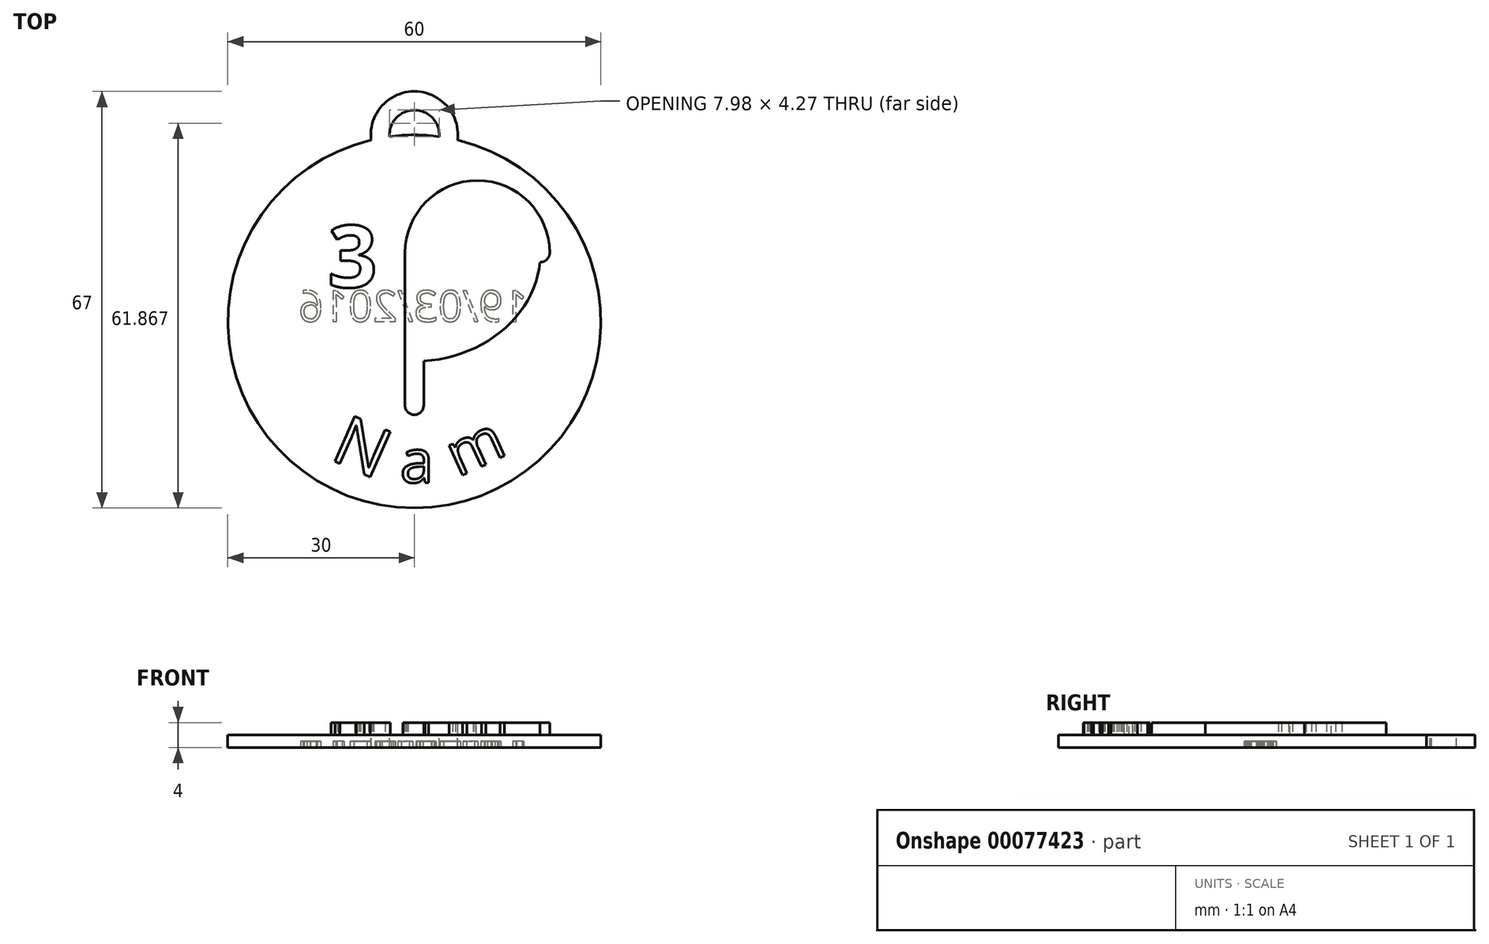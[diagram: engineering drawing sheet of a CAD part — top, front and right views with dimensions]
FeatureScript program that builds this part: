
annotation { "Feature Type Name" : "Feature", "Feature Type Description" : "" }
export const myFeature = defineFeature(function(context is Context, id is Id, definition is map)
    precondition{}
    {
        {
            var Q0;
            Q0=qCreatedBy(makeId("Top.planeOp"),FACE);
            var sketch = newSketch(context, id + "F0", { "sketchPlane" : qUnion([Q0])});
            skCircle(sketch, "E0", {"center": v(0, 0) * mm, "radius": 30 * mm});
            skSolve(sketch);
        }
        {
            var Q0;
            Q0=qSketchRegion(id+"F0",true);
            extrude(context, id + "F1", {"entities" : qUnion([Q0]), "oppositeDirection" : true, "depth" : 2 * mm});
        }
        {
            var Q0;
            Q0=qCreatedBy(makeId("Top.planeOp"),FACE);
            var sketch = newSketch(context, id + "F2", { "sketchPlane" : qUnion([Q0])});
            skEllipticalArc(sketch, "E1", {});
            skLineSegment(sketch, "E2", {"start": v(0, 0) * mm, "end": v(0, 30) * mm, "construction": true});
            skLineSegment(sketch, "E3", {"start": v(0, 11.04) * mm, "end": v(0, -13.5) * mm});
            skArc(sketch, "E4", {"start": v(20.27, 11.04) * mm, "mid": v(10.13, 21.17) * mm, "end": v(0, 11.04) * mm});
            skLineSegment(sketch, "E5", {"start": v(0, 11.04) * mm, "end": v(-16.84, 20.76) * mm, "construction": true});
            skLineSegment(sketch, "E6", {"start": v(0, 11.04) * mm, "end": v(-20.27, 11.04) * mm, "construction": true});
            skArc(sketch, "E7.0.startCap", {"start": v(-1.5, 11.04) * mm, "mid": v(0, 12.54) * mm, "end": v(1.5, 11.04) * mm});
            skArc(sketch, "E7.0.endCap", {"start": v(1.5, -13.5) * mm, "mid": v(0, -15) * mm, "end": v(-1.5, -13.5) * mm});
            skLineSegment(sketch, "E7.0.left", {"start": v(1.5, 11.04) * mm, "end": v(1.5, -13.5) * mm});
            skLineSegment(sketch, "E7.0.right", {"start": v(-1.5, 11.04) * mm, "end": v(-1.5, -13.5) * mm});
            skArc(sketch, "E8.0.startCap", {"start": v(21.77, 11.04) * mm, "mid": v(20.27, 9.54) * mm, "end": v(18.77, 11.04) * mm});
            skArc(sketch, "E8.0.endCap", {"start": v(1.5, 11.04) * mm, "mid": v(0, 9.54) * mm, "end": v(-1.5, 11.04) * mm});
            skArc(sketch, "E8.0.left", {"start": v(18.77, 11.04) * mm, "mid": v(10.13, 19.67) * mm, "end": v(1.5, 11.04) * mm});
            skArc(sketch, "E8.0.right", {"start": v(21.77, 11.04) * mm, "mid": v(10.13, 22.67) * mm, "end": v(-1.5, 11.04) * mm});
            skArc(sketch, "E8.1.startCap", {"start": v(-18.02, 21.68) * mm, "mid": v(-15.91, 21.95) * mm, "end": v(-15.65, 19.84) * mm});
            skArc(sketch, "E8.1.endCap", {"start": v(18.77, 11.04) * mm, "mid": v(20.27, 12.54) * mm, "end": v(21.77, 11.04) * mm});
            skFitSpline(sketch, "E8.1.left", {"points": [v(18.7, 9.5) * mm, v(18.8, 11.04) * mm, v(18.7, 12.6) * mm, v(18.36, 14.63) * mm, v(17.66, 16.6) * mm, v(16.63, 18.49) * mm, v(15.37, 20.3) * mm, v(13.44, 22.32) * mm, v(11.07, 24) * mm, v(8.94, 25.1) * mm, v(6.7, 26.01) * mm, v(4.32, 26.63) * mm, v(1.87, 26.95) * mm, v(0, 27.03) * mm, v(-1.87, 26.95) * mm, v(-4.32, 26.63) * mm, v(-6.7, 26.01) * mm, v(-8.94, 25.1) * mm, v(-11.07, 24) * mm, v(-13.44, 22.32) * mm, v(-15.37, 20.3) * mm, v(-16.63, 18.49) * mm, v(-17.66, 16.6) * mm, v(-18.36, 14.63) * mm, v(-18.7, 12.6) * mm, v(-18.8, 11.04) * mm, v(-18.7, 9.5) * mm, v(-18.36, 7.46) * mm, v(-17.66, 5.48) * mm, v(-16.63, 3.6) * mm, v(-15.37, 1.8) * mm, v(-13.44, -0.24) * mm, v(-11.07, -1.92) * mm, v(-8.94, -3.02) * mm, v(-6.7, -3.93) * mm, v(-4.32, -4.55) * mm, v(-1.87, -4.86) * mm, v(0, -4.94) * mm, v(1.87, -4.86) * mm, v(4.32, -4.55) * mm, v(6.7, -3.93) * mm, v(8.94, -3.02) * mm, v(11.07, -1.92) * mm, v(13.44, -0.24) * mm, v(15.37, 1.8) * mm, v(16.63, 3.6) * mm, v(17.66, 5.48) * mm, v(18.36, 7.46) * mm, v(18.7, 9.5) * mm, v(18.8, 11.04) * mm, v(18.7, 12.6) * mm]});
            skFitSpline(sketch, "E8.1.right", {"points": [v(21.7, 9.15) * mm, v(21.8, 11.04) * mm, v(21.7, 12.93) * mm, v(21.27, 15.42) * mm, v(20.42, 17.81) * mm, v(19.18, 20.07) * mm, v(17.69, 22.22) * mm, v(15.4, 24.61) * mm, v(12.65, 26.56) * mm, v(10.2, 27.83) * mm, v(7.62, 28.88) * mm, v(4.92, 29.58) * mm, v(2.12, 29.94) * mm, v(0, 30.03) * mm, v(-2.12, 29.94) * mm, v(-4.92, 29.58) * mm, v(-7.62, 28.88) * mm, v(-10.2, 27.83) * mm, v(-12.65, 26.56) * mm, v(-15.4, 24.61) * mm, v(-17.69, 22.22) * mm, v(-19.18, 20.07) * mm, v(-20.42, 17.81) * mm, v(-21.27, 15.42) * mm, v(-21.7, 12.93) * mm, v(-21.8, 11.04) * mm, v(-21.7, 9.15) * mm, v(-21.27, 6.67) * mm, v(-20.42, 4.27) * mm, v(-19.18, 2) * mm, v(-17.69, -0.14) * mm, v(-15.4, -2.53) * mm, v(-12.65, -4.48) * mm, v(-10.2, -5.75) * mm, v(-7.62, -6.8) * mm, v(-4.92, -7.5) * mm, v(-2.12, -7.86) * mm, v(0, -7.95) * mm, v(2.12, -7.86) * mm, v(4.92, -7.5) * mm, v(7.62, -6.8) * mm, v(10.2, -5.75) * mm, v(12.65, -4.48) * mm, v(15.4, -2.53) * mm, v(17.69, -0.14) * mm, v(19.18, 2) * mm, v(20.42, 4.27) * mm, v(21.27, 6.67) * mm, v(21.7, 9.15) * mm, v(21.8, 11.04) * mm, v(21.7, 12.93) * mm]});
            const initialGuessF2  = {"E1": [0, 0.011041626236194823, 1, 0, 0.020266667008310185, 0.017458373763805178, 2.5511335140588507, 0]};
            skSetInitialGuess(sketch, initialGuessF2);
            skSolve(sketch);
        }
        {
            var Q0;
            {var subQ0=sQuery(id+"F2.wireOp",EDGE,"E8.1.startCap");Q0=makeQuery(id+"F2.imprint","IMPRINT",FACE,{"disambiguationData":[TD([[makeQuery(id+"F2.imprint","IMPRINT",EDGE,{"derivedFrom":subQ0}),-1.0]])]});}
            var Q1;
            {var subQ0=sQuery(id+"F2.wireOp",EDGE,"E7.0.right");var subQ1=sQuery(id+"F2.wireOp",EDGE,"E1");var subQ2=makeQuery(id+"F2.imprint","INTERSECT",VERTEX,{"derivedFrom":[subQ1,subQ0]});Q1=makeQuery(id+"F2.imprint","IMPRINT",FACE,{"disambiguationData":[TD([[makeQuery(id+"F2.imprint","IMPRINT",EDGE,{"disambiguationData":[TD([[subQ2,-1.0]])],"derivedFrom":subQ1}),1.0]])]});}
            var Q2;
            {var subQ0=sQuery(id+"F2.wireOp",EDGE,"E3");var subQ1=sQuery(id+"F2.wireOp",EDGE,"E1");var subQ2=makeQuery(id+"F2.imprint","INTERSECT",VERTEX,{"derivedFrom":[subQ1,subQ0]});Q2=makeQuery(id+"F2.imprint","IMPRINT",FACE,{"disambiguationData":[TD([[makeQuery(id+"F2.imprint","IMPRINT",EDGE,{"disambiguationData":[TD([[subQ2,-1.0]])],"derivedFrom":subQ1}),1.0]])]});}
            var Q3;
            {var subQ0=sQuery(id+"F2.wireOp",EDGE,"E7.0.right");var subQ1=sQuery(id+"F2.wireOp",EDGE,"E1");var subQ2=makeQuery(id+"F2.imprint","INTERSECT",VERTEX,{"derivedFrom":[subQ1,subQ0]});Q3=makeQuery(id+"F2.imprint","IMPRINT",FACE,{"disambiguationData":[TD([[makeQuery(id+"F2.imprint","IMPRINT",EDGE,{"disambiguationData":[TD([[subQ2,-1.0]])],"derivedFrom":subQ1}),-1.0]])]});}
            var Q4;
            {var subQ0=sQuery(id+"F2.wireOp",EDGE,"E3");var subQ1=sQuery(id+"F2.wireOp",EDGE,"E1");var subQ2=makeQuery(id+"F2.imprint","INTERSECT",VERTEX,{"derivedFrom":[subQ1,subQ0]});Q4=makeQuery(id+"F2.imprint","IMPRINT",FACE,{"disambiguationData":[TD([[makeQuery(id+"F2.imprint","IMPRINT",EDGE,{"disambiguationData":[TD([[subQ2,-1.0]])],"derivedFrom":subQ1}),-1.0]])]});}
            var Q5;
            {var subQ0=sQuery(id+"F2.wireOp",EDGE,"E7.0.left");var subQ1=sQuery(id+"F2.wireOp",EDGE,"E1");var subQ2=makeQuery(id+"F2.imprint","INTERSECT",VERTEX,{"derivedFrom":[subQ1,subQ0]});Q5=makeQuery(id+"F2.imprint","IMPRINT",FACE,{"disambiguationData":[TD([[makeQuery(id+"F2.imprint","IMPRINT",EDGE,{"disambiguationData":[TD([[subQ2,-1.0]])],"derivedFrom":subQ1}),-1.0]])]});}
            var Q6;
            {var subQ0=sQuery(id+"F2.wireOp",EDGE,"E7.0.left");var subQ1=sQuery(id+"F2.wireOp",EDGE,"E1");var subQ2=makeQuery(id+"F2.imprint","INTERSECT",VERTEX,{"derivedFrom":[subQ1,subQ0]});Q6=makeQuery(id+"F2.imprint","IMPRINT",FACE,{"disambiguationData":[TD([[makeQuery(id+"F2.imprint","IMPRINT",EDGE,{"disambiguationData":[TD([[subQ2,-1.0]])],"derivedFrom":subQ1}),1.0]])]});}
            var Q7;
            {var subQ0=sQuery(id+"F2.wireOp",EDGE,"E4");var subQ1=sQuery(id+"F2.wireOp",EDGE,"E1");var subQ2=makeQuery(id+"F2.imprint","INTERSECT",VERTEX,{"derivedFrom":[subQ1,subQ0]});Q7=makeQuery(id+"F2.imprint","IMPRINT",FACE,{"disambiguationData":[TD([[makeQuery(id+"F2.imprint","IMPRINT",EDGE,{"disambiguationData":[TD([[subQ2,1.0]])],"derivedFrom":subQ1}),-1.0]])]});}
            var Q8;
            {var subQ0=sQuery(id+"F2.wireOp",EDGE,"E4");var subQ1=sQuery(id+"F2.wireOp",EDGE,"E1");var subQ2=makeQuery(id+"F2.imprint","INTERSECT",VERTEX,{"derivedFrom":[subQ1,subQ0]});Q8=makeQuery(id+"F2.imprint","IMPRINT",FACE,{"disambiguationData":[TD([[makeQuery(id+"F2.imprint","IMPRINT",EDGE,{"disambiguationData":[TD([[subQ2,1.0]])],"derivedFrom":subQ1}),1.0]])]});}
            var Q9;
            {var subQ5=sQuery(id+"F2.wireOp",EDGE,"E8.0.left");Q9=makeQuery(id+"F2.imprint","IMPRINT",FACE,{"disambiguationData":[TD([[makeQuery(id+"F2.imprint","IMPRINT",EDGE,{"derivedFrom":subQ5}),-1.0]])]});}
            var Q10;
            {var subQ5=sQuery(id+"F2.wireOp",EDGE,"E8.0.right");Q10=makeQuery(id+"F2.imprint","IMPRINT",FACE,{"disambiguationData":[TD([[makeQuery(id+"F2.imprint","IMPRINT",EDGE,{"derivedFrom":subQ5}),1.0]])]});}
            var Q11;
            {var subQ0=sQuery(id+"F2.wireOp",EDGE,"E4");var subQ1=sQuery(id+"F2.wireOp",EDGE,"E3");var subQ2=makeQuery(id+"F2.imprint","INTERSECT",VERTEX,{"derivedFrom":[subQ1,subQ0]});Q11=makeQuery(id+"F2.imprint","IMPRINT",FACE,{"disambiguationData":[TD([[makeQuery(id+"F2.imprint","IMPRINT",EDGE,{"disambiguationData":[TD([[subQ2,-1.0]])],"derivedFrom":subQ1}),-1.0]])]});}
            var Q12;
            {var subQ0=sQuery(id+"F2.wireOp",EDGE,"E4");var subQ1=sQuery(id+"F2.wireOp",EDGE,"E3");var subQ2=makeQuery(id+"F2.imprint","INTERSECT",VERTEX,{"derivedFrom":[subQ1,subQ0]});Q12=makeQuery(id+"F2.imprint","IMPRINT",FACE,{"disambiguationData":[TD([[makeQuery(id+"F2.imprint","IMPRINT",EDGE,{"disambiguationData":[TD([[subQ2,-1.0]])],"derivedFrom":subQ1}),1.0]])]});}
            var Q13;
            {var subQ0=sQuery(id+"F2.wireOp",EDGE,"E8.0.endCap");var subQ1=sQuery(id+"F2.wireOp",EDGE,"E3");var subQ2=makeQuery(id+"F2.imprint","INTERSECT",VERTEX,{"derivedFrom":[subQ1,subQ0]});Q13=makeQuery(id+"F2.imprint","IMPRINT",FACE,{"disambiguationData":[TD([[makeQuery(id+"F2.imprint","IMPRINT",EDGE,{"disambiguationData":[TD([[subQ2,-1.0]])],"derivedFrom":subQ1}),-1.0]])]});}
            var Q14;
            {var subQ0=sQuery(id+"F2.wireOp",EDGE,"E8.0.endCap");var subQ1=sQuery(id+"F2.wireOp",EDGE,"E3");var subQ2=makeQuery(id+"F2.imprint","INTERSECT",VERTEX,{"derivedFrom":[subQ1,subQ0]});Q14=makeQuery(id+"F2.imprint","IMPRINT",FACE,{"disambiguationData":[TD([[makeQuery(id+"F2.imprint","IMPRINT",EDGE,{"disambiguationData":[TD([[subQ2,-1.0]])],"derivedFrom":subQ1}),1.0]])]});}
            var Q15;
            {var subQ1=sQuery(id+"F2.wireOp",EDGE,"E7.0.endCap");Q15=makeQuery(id+"F2.imprint","IMPRINT",FACE,{"disambiguationData":[TD([[makeQuery(id+"F2.imprint","IMPRINT",EDGE,{"derivedFrom":subQ1}),-1.0]])]});}
            extrude(context, id + "F3", {"entities" : qUnion([Q0, Q1, Q2, Q3, Q4, Q5, Q6, Q7, Q8, Q9, Q10, Q11, Q12, Q13, Q14, Q15]), "operationType" : NewBodyOperationType.ADD, "depth" : 2 * mm});
        }
        {
            var Q0;
            Q0=qCreatedBy(makeId("Top.planeOp"),FACE);
            var sketch = newSketch(context, id + "F4", { "sketchPlane" : qUnion([Q0])});
            skText(sketch, "E9", { "text": "3", "fontName": "OpenSans-Bold.ttf"});
            skText(sketch, "E10", { "text": "D", "fontName": "OpenSans-Bold.ttf"});
            const initialGuessF4  = {"E9": [-0.0139, 0.0055, 1, 0, 0.01], "E10": [0.0055, 0.0055, 1, 0, 0.01]};
            skSetInitialGuess(sketch, initialGuessF4);
            skSolve(sketch);
        }
        {
            var Q0;
            Q0=qSketchRegion(id+"F4",true);
            extrude(context, id + "F5", {"entities" : qUnion([Q0]), "operationType" : NewBodyOperationType.ADD, "depth" : 2 * mm});
        }
        {
            var Q0;
            {var subQ8=sQuery(id+"F0.wireOp",EDGE,"E0");Q0=makeQuery(id+"F3.boolean.opBoolean","SPLIT",FACE,{"disambiguationData":[TD([makeQuery(id+"F1.opExtrude","SWEPT_FACE",FACE,{"disambiguationData":[OSD([subQ8])]})])],"derivedFrom":makeQuery(id+"F1.opExtrude","CAP_FACE",FACE,{"disambiguationData":[OSD([subQ8])],"isStart":true})});}
            var sketch = newSketch(context, id + "F6", { "sketchPlane" : qUnion([Q0])});
            skCircle(sketch, "E11.0", {"center": v(0, 0) * mm, "radius": 26 * mm, "construction": true});
            skText(sketch, "E12", { "text": "N", "fontName": "OpenSans-Regular.ttf"});
            skText(sketch, "E13", { "text": "a", "fontName": "OpenSans-Regular.ttf"});
            skText(sketch, "E14", { "text": "m", "fontName": "OpenSans-Regular.ttf"});
            const initialGuessF6  = {"E12": [-0.01377, -0.02205, 0.9141, -0.40551, 0.008], "E13": [-0.0023, -0.0259, 1, 0, 0.007], "E14": [0.007, -0.02504, 0.90827, 0.41838, 0.007]};
            skSetInitialGuess(sketch, initialGuessF6);
            skSolve(sketch);
        }
        {
            var Q0;
            Q0=qSketchRegion(id+"F6",true);
            extrude(context, id + "F7", {"entities" : qUnion([Q0]), "operationType" : NewBodyOperationType.ADD, "depth" : 2 * mm});
        }
        {
            var Q0;
            Q0=qCreatedBy(makeId("Top.planeOp"),FACE);
            var sketch = newSketch(context, id + "F8", { "sketchPlane" : qUnion([Q0])});
            skArc(sketch, "E15", {"start": v(5.48, 29.5) * mm, "mid": v(0, 35.5) * mm, "end": v(-5.48, 29.5) * mm});
            skArc(sketch, "E16.0.startCap", {"start": v(6.97, 29.36) * mm, "mid": v(5.34, 28) * mm, "end": v(3.98, 29.63) * mm});
            skArc(sketch, "E16.0.endCap", {"start": v(-3.98, 29.63) * mm, "mid": v(-5.34, 28) * mm, "end": v(-6.97, 29.36) * mm});
            skArc(sketch, "E16.0.left", {"start": v(3.98, 29.63) * mm, "mid": v(0, 34) * mm, "end": v(-3.98, 29.63) * mm});
            skArc(sketch, "E16.0.right", {"start": v(6.97, 29.36) * mm, "mid": v(0, 37) * mm, "end": v(-6.97, 29.36) * mm});
            skSolve(sketch);
        }
        {
            var Q0;
            Q0=qSketchRegion(id+"F8",true);
            extrude(context, id + "F9", {"entities" : qUnion([Q0]), "operationType" : NewBodyOperationType.ADD, "oppositeDirection" : true, "depth" : 2 * mm});
        }
        {
            var Q0;
            Q0=makeQuery(id+"F9.boolean.opBoolean","MERGE",FACE,{"derivedFrom":[makeQuery(id+"F1.opExtrude","CAP_FACE",FACE,{"disambiguationData":[OSD([sQuery(id+"F0.wireOp",EDGE,"E0")])],"isStart":false}),makeQuery(id+"F9.opExtrude","CAP_FACE",FACE,{"disambiguationData":[OSD([sQuery(id+"F8.wireOp",EDGE,"E16.0.startCap"),sQuery(id+"F8.wireOp",EDGE,"E16.0.endCap"),sQuery(id+"F8.wireOp",EDGE,"E16.0.left"),sQuery(id+"F8.wireOp",EDGE,"E16.0.right")])],"isStart":false})]});
            var sketch = newSketch(context, id + "F10", { "sketchPlane" : qUnion([Q0])});
            skText(sketch, "E17", { "text": "19/03/2016", "fontName": "OpenSans-Regular.ttf"});
            const initialGuessF10  = {"E17": [0.01826, 0, -1, 0, 0.005]};
            skSetInitialGuess(sketch, initialGuessF10);
            skSolve(sketch);
        }
        {
            var Q0;
            Q0=qSketchRegion(id+"F10",true);
            extrude(context, id + "F11", {"entities" : qUnion([Q0]), "operationType" : NewBodyOperationType.REMOVE, "oppositeDirection" : true, "depth" : 1 * mm});
        }
    });
